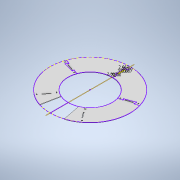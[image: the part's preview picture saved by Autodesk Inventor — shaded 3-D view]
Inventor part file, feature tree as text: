
AUTODESK INVENTOR PART (.ipt)
format: ipt  version: 2020 (Build 240168000, 168)  size: 435,712 bytes
history: native  units: mm
features: extrude x4, sketch x4, pattern_circular x3, mirror x2
ambient origin geometry x8: Origin, YZ Plane, XZ Plane, XY Plane, X Axis, Y Axis, Z Axis, Center Point
bodies: Body1 (feature_tree)
feature tree (13):
  extrude  "Extrusion3"  Depth=6.5mm
  extrude  "Extrusion4"  Depth=2.666667mm
  sketch  "Sketch3"  dims[d24=2.666667mm d25=2.666667mm]
  sketch  "Sketch5"  dims[d32=1.333333mm d33=1.333333mm]
  extrude  "Extrusion7"  Depth=1.333333mm
  pattern_circular  "Circular Pattern2"  [2 undecoded]
  pattern_circular  "Circular Pattern3"  [2 undecoded]
  mirror  "Mirror3"
  extrude  "Extrusion10"  Depth=0.5mm
  mirror  "Mirror4"
  pattern_circular  "Circular Pattern4"  [2 undecoded]
  sketch  "Sketch2"  dims[d15=6.0mm d16=0.0mm d21=6.5mm]
  sketch  "Sketch6"  dims[d38=0.0mm d39=0.0mm d40=3.25mm d52=4.363323mm d60=0.872665mm d61=12.566371mm d62=13.439035mm d63=2.666667mm d64=0.523599mm d66=0.523599mm d67=2.666667mm d68=2.666667mm d70=12.566371mm d71=12.566371mm d84=467.42mm d85=850.0mm d86=658.71mm d87=150.07mm d88=425.0mm d89=4.363323mm d90=1.919862mm d91=1.919862mm d104=6.5mm d105=12.0mm d108=1.333333mm d109=1.333333mm d110=1.333333mm d111=1.333333mm d112=0.0mm d113=0.0mm d114=0.0mm d145=20.0mm d146=12.566371mm d149=145.0mm d150=90.0deg d151=90.0deg d152=90.0deg d153=90.0deg d154=20.0mm d155=25.132741mm d157=10.0mm d158=0.0mm d162=70.0mm d163=294.355mm d165=3.25mm d174=20.0mm d175=25.132741mm d176=0.5mm d177=0.872665mm]
note: 6 required parameter values undecoded (feature->parameter linkage not recoverable at this tier; creation-order binding heuristic only, values carry confidence <= 0.55)
